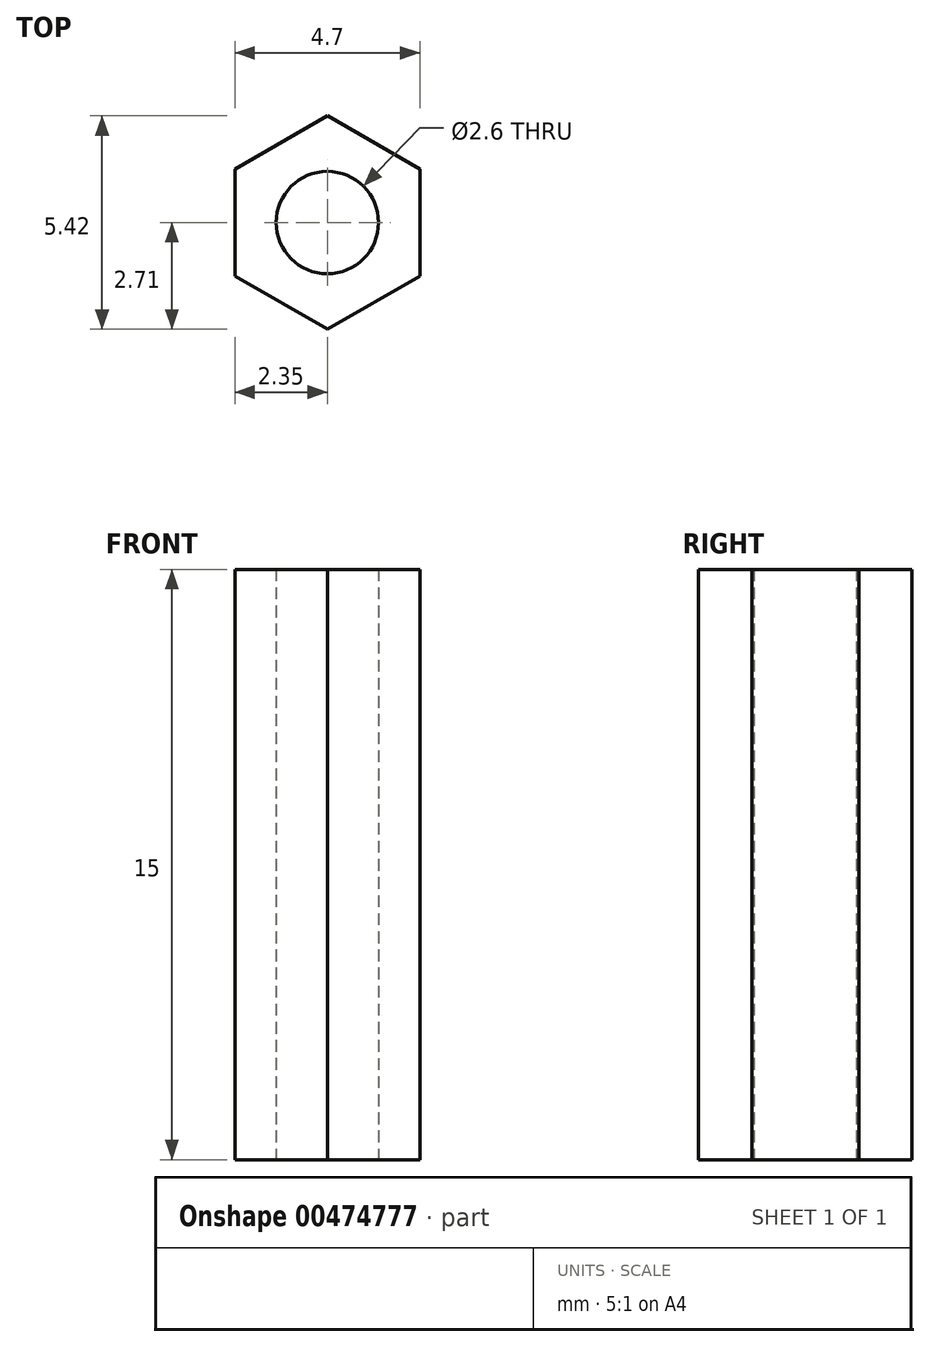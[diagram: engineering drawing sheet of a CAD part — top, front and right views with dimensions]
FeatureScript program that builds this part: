
annotation { "Feature Type Name" : "Feature", "Feature Type Description" : "" }
export const myFeature = defineFeature(function(context is Context, id is Id, definition is map)
    precondition{}
    {
        {
            var Q0;
            Q0=qCreatedBy(makeId("Top.planeOp"),FACE);
            var sketch = newSketch(context, id + "F0", { "sketchPlane" : qUnion([Q0])});
            skCircle(sketch, "E0.cCircle", {"center": v(0, 0) * mm, "radius": 2.35 * mm, "construction": true});
            skLineSegment(sketch, "E0.0", {"start": v(2.35, 1.36) * mm, "end": v(2.35, -1.36) * mm});
            skLineSegment(sketch, "E0.1", {"start": v(2.35, -1.36) * mm, "end": v(0, -2.71) * mm});
            skLineSegment(sketch, "E0.2", {"start": v(0, -2.71) * mm, "end": v(-2.35, -1.36) * mm});
            skLineSegment(sketch, "E0.3", {"start": v(-2.35, -1.36) * mm, "end": v(-2.35, 1.36) * mm});
            skLineSegment(sketch, "E0.4", {"start": v(-2.35, 1.36) * mm, "end": v(0, 2.71) * mm});
            skLineSegment(sketch, "E0.5", {"start": v(0, 2.71) * mm, "end": v(2.35, 1.36) * mm});
            skPoint(sketch, "E0.0.midPoint", {"position": v(2.35, 0) * mm});
            skCircle(sketch, "E1", {"center": v(0, 0) * mm, "radius": 1.3 * mm});
            skSolve(sketch);
        }
        {
            var Q0;
            Q0 = qSketchRegion(id + "F0", true);
            extrude(context, id + "F1", {"entities" : qUnion([Q0]), "depth" : 15 * mm});
        }
    });
